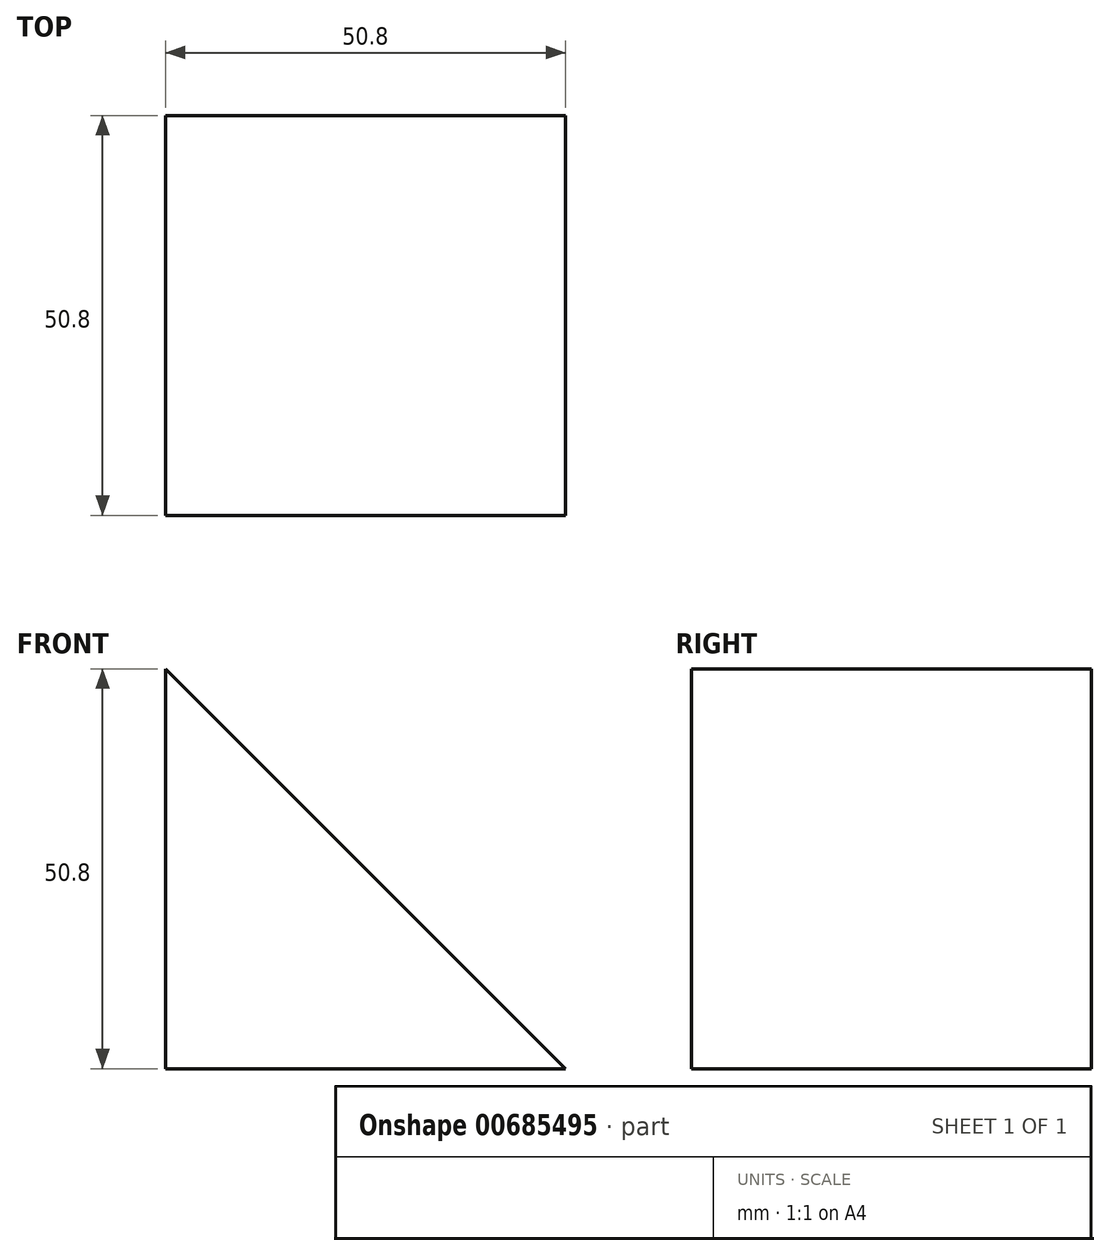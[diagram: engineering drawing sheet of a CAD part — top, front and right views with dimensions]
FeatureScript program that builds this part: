
annotation { "Feature Type Name" : "Feature", "Feature Type Description" : "" }
export const myFeature = defineFeature(function(context is Context, id is Id, definition is map)
    precondition{}
    {
        {
            var Q0;
            Q0=qCreatedBy(makeId("Front.planeOp"),FACE);
            var sketch = newSketch(context, id + "F0", { "sketchPlane" : qUnion([Q0])});
            skLineSegment(sketch, "E0", {"start": v(-44.2, 53.19) * mm, "end": v(-44.2, 2.39) * mm});
            skLineSegment(sketch, "E1", {"start": v(-44.2, 2.39) * mm, "end": v(6.6, 2.39) * mm});
            skLineSegment(sketch, "E2", {"start": v(6.6, 2.39) * mm, "end": v(-44.2, 53.19) * mm});
            skSolve(sketch);
        }
        {
            var Q0;
            Q0 = qSketchRegion(id + "F0", true);
            extrude(context, id + "F1", {"entities" : qUnion([Q0]), "depth" : 50.8 * mm, "offsetDistance" : 25.4 * mm});
        }
    });
